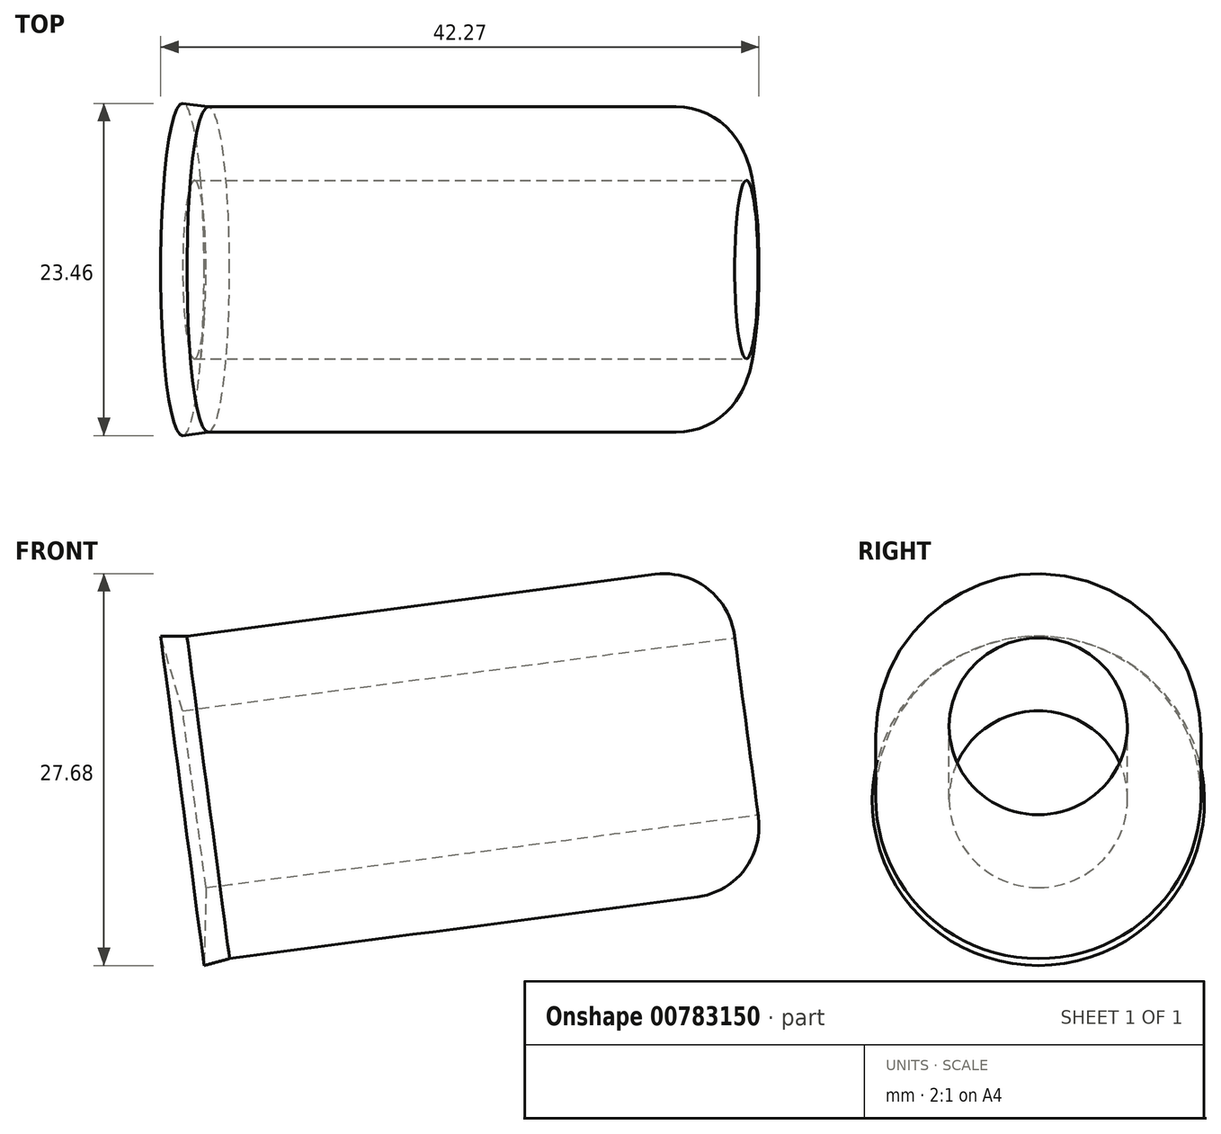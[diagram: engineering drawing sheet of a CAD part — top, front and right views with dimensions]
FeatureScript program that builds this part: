
annotation { "Feature Type Name" : "Feature", "Feature Type Description" : "" }
export const myFeature = defineFeature(function(context is Context, id is Id, definition is map)
    precondition{}
    {
        {
            var Q0;
            Q0=qCreatedBy(makeId("Front.planeOp"),FACE);
            var sketch = newSketch(context, id + "F0", { "sketchPlane" : qUnion([Q0])});
            skLineSegment(sketch, "E0", {"start": v(-24.74, 5.15) * mm, "end": v(-22.88, 5.15) * mm});
            skLineSegment(sketch, "E1", {"start": v(-22.88, 5.15) * mm, "end": v(10.18, 9.51) * mm});
            skLineSegment(sketch, "E2", {"start": v(15.79, 5.2) * mm, "end": v(15.81, 5.02) * mm});
            skLineSegment(sketch, "E3", {"start": v(15.81, 5.02) * mm, "end": v(-23.18, -0.13) * mm});
            skLineSegment(sketch, "E4", {"start": v(-23.18, -0.13) * mm, "end": v(-24.74, 5.15) * mm});
            skLineSegment(sketch, "E5", {"start": v(17.92, -1.05) * mm, "end": v(-26.44, -6.91) * mm});
            skPoint(sketch, "E6.visualSharp", {"position": v(15.13, 10.17) * mm});
            skArc(sketch, "E6.filletArc", {"start": v(15.79, 5.2) * mm, "mid": v(13.87, 8.52) * mm, "end": v(10.18, 9.51) * mm});
            skSolve(sketch);
        }
        {
            var Q0;
            Q0 = qSketchRegion(id + "F0", true);
            var Q1;
            Q1=sQuery(id+"F0.wireOp",EDGE,"E5");
            revolve(context, id + "F1", {"surfaceOperationType" : NewSurfaceOperationType.NEW, "entities" : qUnion([Q0]), "axis" : qUnion([Q1]), "revolveType" : RevolveType.FULL});
        }
    });
